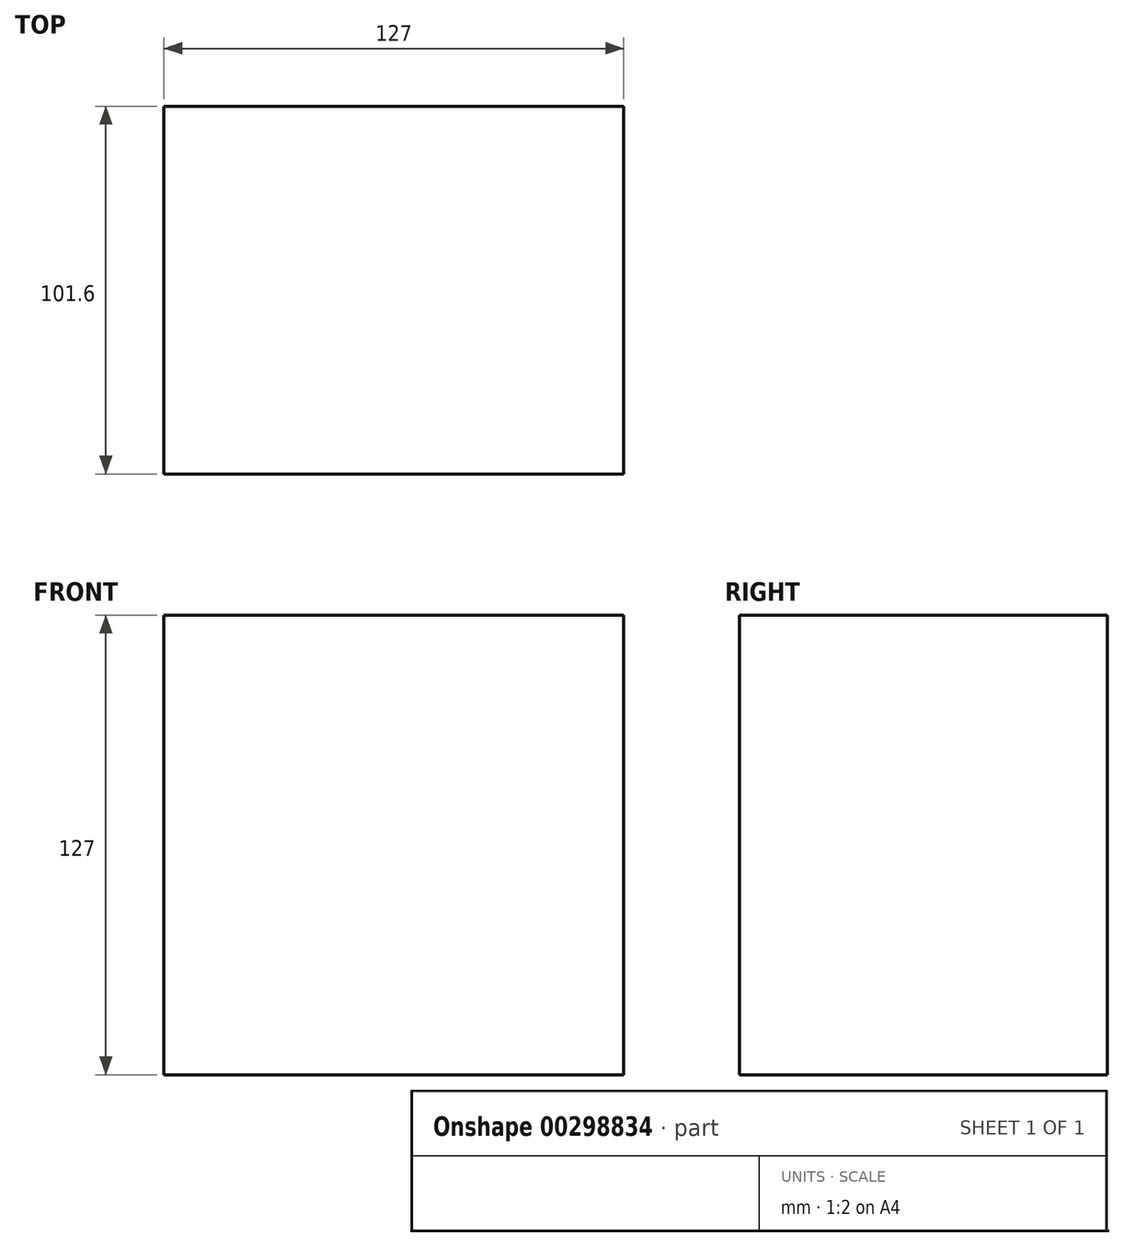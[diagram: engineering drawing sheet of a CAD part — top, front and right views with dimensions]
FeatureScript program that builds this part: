
annotation { "Feature Type Name" : "Feature", "Feature Type Description" : "" }
export const myFeature = defineFeature(function(context is Context, id is Id, definition is map)
    precondition{}
    {
        {
            var Q0;
            Q0=qCreatedBy(makeId("Front.planeOp"),FACE);
            var sketch = newSketch(context, id + "F0", { "sketchPlane" : qUnion([Q0])});
            skLineSegment(sketch, "E0.bottom", {"start": v(-63.5, 63.5) * mm, "end": v(63.5, 63.5) * mm});
            skLineSegment(sketch, "E0.top", {"start": v(-63.5, -63.5) * mm, "end": v(63.5, -63.5) * mm});
            skLineSegment(sketch, "E0.left", {"start": v(-63.5, 63.5) * mm, "end": v(-63.5, -63.5) * mm});
            skLineSegment(sketch, "E0.right", {"start": v(63.5, 63.5) * mm, "end": v(63.5, -63.5) * mm});
            skPoint(sketch, "E0.middle", {"position": v(0, 0) * mm});
            skSolve(sketch);
        }
        {
            var Q0;
            Q0=makeQuery(id+"F0.imprint","IMPRINT",FACE,{"disambiguationData":[TD([[makeQuery(id+"F0.imprint","IMPRINT",EDGE,{"derivedFrom":sQuery(id+"F0.wireOp",EDGE,"E0.bottom")}),-1.0]])]});
            extrude(context, id + "F1", {"entities" : qUnion([Q0]), "depth" : 101.6 * mm});
        }
    });
